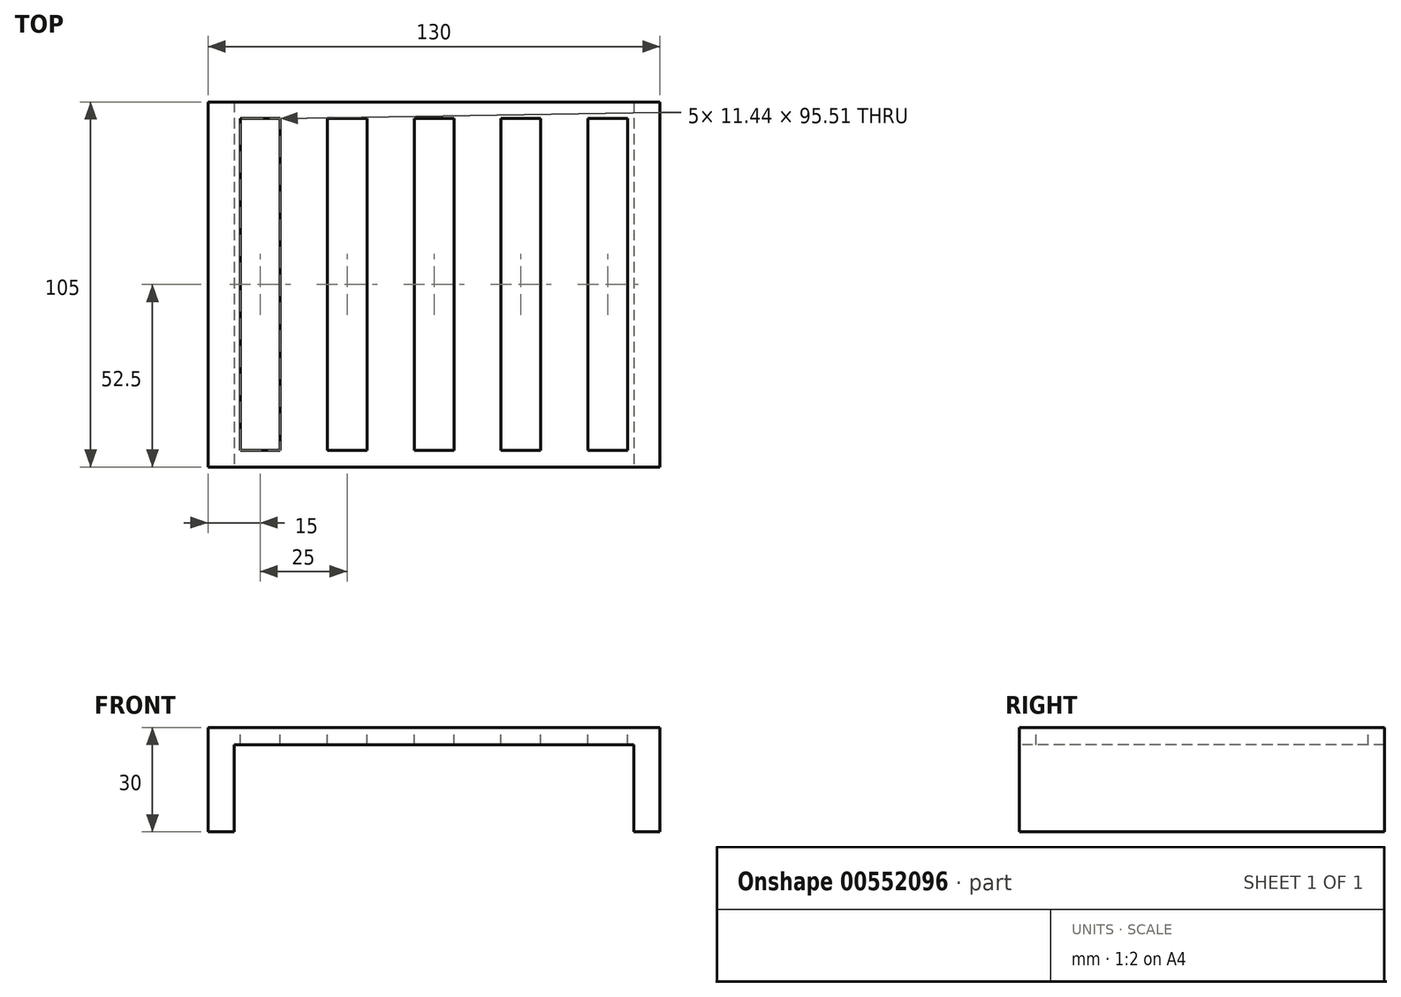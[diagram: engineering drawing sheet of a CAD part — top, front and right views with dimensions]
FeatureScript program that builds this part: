
annotation { "Feature Type Name" : "Feature", "Feature Type Description" : "" }
export const myFeature = defineFeature(function(context is Context, id is Id, definition is map)
    precondition{}
    {
        {
            var Q0;
            Q0=qCreatedBy(makeId("Top.planeOp"),FACE);
            var sketch = newSketch(context, id + "F0", { "sketchPlane" : qUnion([Q0])});
            skLineSegment(sketch, "E0.bottom", {"start": v(-65, 52.5) * mm, "end": v(65, 52.5) * mm});
            skLineSegment(sketch, "E0.top", {"start": v(-65, -52.5) * mm, "end": v(65, -52.5) * mm});
            skLineSegment(sketch, "E0.left", {"start": v(-65, 52.5) * mm, "end": v(-65, -52.5) * mm});
            skLineSegment(sketch, "E0.right", {"start": v(65, 52.5) * mm, "end": v(65, -52.5) * mm});
            skPoint(sketch, "E0.middle", {"position": v(0, 0) * mm});
            skSolve(sketch);
        }
        {
            var Q0;
            Q0=makeQuery(id+"F0.imprint","IMPRINT",FACE,{"disambiguationData":[TD([[makeQuery(id+"F0.imprint","IMPRINT",EDGE,{"derivedFrom":sQuery(id+"F0.wireOp",EDGE,"E0.bottom")}),-1.0]])]});
            extrude(context, id + "F1", {"entities" : qUnion([Q0]), "depth" : 5 * mm, "offsetDistance" : 25 * mm});
        }
        {
            var Q0;
            Q0=makeQuery(id+"F1.opExtrude","CAP_FACE",FACE,{"disambiguationData":[OSD([sQuery(id+"F0.wireOp",EDGE,"E0.bottom"),sQuery(id+"F0.wireOp",EDGE,"E0.top"),sQuery(id+"F0.wireOp",EDGE,"E0.left"),sQuery(id+"F0.wireOp",EDGE,"E0.right")])],"isStart":false});
            var sketch = newSketch(context, id + "F2", { "sketchPlane" : qUnion([Q0])});
            skSolve(sketch);
        }
        {
            var Q0;
            Q0=makeQuery(id+"F1.opExtrude","CAP_FACE",FACE,{"disambiguationData":[OSD([sQuery(id+"F0.wireOp",EDGE,"E0.bottom"),sQuery(id+"F0.wireOp",EDGE,"E0.top"),sQuery(id+"F0.wireOp",EDGE,"E0.left"),sQuery(id+"F0.wireOp",EDGE,"E0.right")])],"isStart":true});
            var sketch = newSketch(context, id + "F3", { "sketchPlane" : qUnion([Q0])});
            skLineSegment(sketch, "E1.bottom", {"start": v(57.5, -33.84) * mm, "end": v(-57.5, -33.84) * mm});
            skLineSegment(sketch, "E1.top", {"start": v(57.5, 33.84) * mm, "end": v(-57.5, 33.84) * mm});
            skLineSegment(sketch, "E1.left", {"start": v(57.5, -33.84) * mm, "end": v(57.5, 33.84) * mm});
            skLineSegment(sketch, "E1.right", {"start": v(-57.5, -33.84) * mm, "end": v(-57.5, 33.84) * mm});
            skPoint(sketch, "E1.middle", {"position": v(0, 0) * mm});
            skLineSegment(sketch, "E2.bottom", {"start": v(65, -52.5) * mm, "end": v(57.5, -52.5) * mm});
            skLineSegment(sketch, "E2.top", {"start": v(65, 52.5) * mm, "end": v(57.5, 52.5) * mm});
            skLineSegment(sketch, "E2.left", {"start": v(65, -52.5) * mm, "end": v(65, 52.5) * mm});
            skLineSegment(sketch, "E2.right", {"start": v(57.5, -52.5) * mm, "end": v(57.5, 52.5) * mm});
            skLineSegment(sketch, "E3.bottom", {"start": v(-65, -52.5) * mm, "end": v(-57.5, -52.5) * mm});
            skLineSegment(sketch, "E3.top", {"start": v(-65, 52.5) * mm, "end": v(-57.5, 52.5) * mm});
            skLineSegment(sketch, "E3.left", {"start": v(-65, -52.5) * mm, "end": v(-65, 52.5) * mm});
            skLineSegment(sketch, "E3.right", {"start": v(-57.5, -52.5) * mm, "end": v(-57.5, 52.5) * mm});
            skSolve(sketch);
        }
        {
            var Q0;
            {var subQ2=sQuery(id+"F3.wireOp",EDGE,"E2.bottom");Q0=makeQuery(id+"F3.imprint","IMPRINT",FACE,{"disambiguationData":[TD([[makeQuery(id+"F3.imprint","IMPRINT",EDGE,{"derivedFrom":subQ2}),1.0]])]});}
            var Q1;
            {var subQ2=sQuery(id+"F3.wireOp",EDGE,"E3.bottom");Q1=makeQuery(id+"F3.imprint","IMPRINT",FACE,{"disambiguationData":[TD([[makeQuery(id+"F3.imprint","IMPRINT",EDGE,{"derivedFrom":subQ2}),1.0]])]});}
            extrude(context, id + "F4", {"entities" : qUnion([Q0, Q1]), "operationType" : NewBodyOperationType.ADD, "depth" : 25 * mm, "offsetDistance" : 25 * mm});
        }
        {
            var Q0;
            Q0=makeQuery(id+"F2.imprint","IMPRINT",FACE,{"disambiguationData":[TD([[makeQuery(id+"F2.imprint","IMPRINT",EDGE,{"derivedFrom":makeQuery(id+"F1.opExtrude","CAP_EDGE",EDGE,{"disambiguationData":[OSD([sQuery(id+"F0.wireOp",EDGE,"E0.bottom")])],"isStart":false})}),-1.0]])]});
            var sketch = newSketch(context, id + "F5", { "sketchPlane" : qUnion([Q0])});
            skLineSegment(sketch, "E4.bottom", {"start": v(-5.72, 47.76) * mm, "end": v(5.72, 47.76) * mm});
            skLineSegment(sketch, "E4.top", {"start": v(-5.72, -47.76) * mm, "end": v(5.72, -47.76) * mm});
            skLineSegment(sketch, "E4.left", {"start": v(-5.72, 47.76) * mm, "end": v(-5.72, -47.76) * mm});
            skLineSegment(sketch, "E4.right", {"start": v(5.72, 47.76) * mm, "end": v(5.72, -47.76) * mm});
            skPoint(sketch, "E4.middle", {"position": v(0, 0) * mm});
            skLineSegment(sketch, "E5.1.0.0", {"start": v(30.72, 47.76) * mm, "end": v(30.72, -47.76) * mm});
            skLineSegment(sketch, "E5.1.0.1", {"start": v(19.28, 47.76) * mm, "end": v(19.28, -47.76) * mm});
            skLineSegment(sketch, "E5.1.0.2", {"start": v(19.28, 47.76) * mm, "end": v(30.72, 47.76) * mm});
            skLineSegment(sketch, "E5.1.0.3", {"start": v(19.28, -47.76) * mm, "end": v(30.72, -47.76) * mm});
            skLineSegment(sketch, "E5.2.0.0", {"start": v(55.72, 47.76) * mm, "end": v(55.72, -47.76) * mm});
            skLineSegment(sketch, "E5.2.0.1", {"start": v(44.28, 47.76) * mm, "end": v(44.28, -47.76) * mm});
            skLineSegment(sketch, "E5.2.0.2", {"start": v(44.28, 47.76) * mm, "end": v(55.72, 47.76) * mm});
            skLineSegment(sketch, "E5.2.0.3", {"start": v(44.28, -47.76) * mm, "end": v(55.72, -47.76) * mm});
            skLineSegment(sketch, "E5.direction1", {"start": v(5.72, -47.76) * mm, "end": v(30.72, -47.76) * mm, "construction": true});
            skLineSegment(sketch, "E6.1.0.0", {"start": v(-30.72, 47.76) * mm, "end": v(-30.72, -47.76) * mm});
            skLineSegment(sketch, "E6.1.0.1", {"start": v(-19.28, 47.76) * mm, "end": v(-19.28, -47.76) * mm});
            skLineSegment(sketch, "E6.1.0.2", {"start": v(-30.72, -47.76) * mm, "end": v(-19.28, -47.76) * mm});
            skLineSegment(sketch, "E6.1.0.3", {"start": v(-30.72, 47.76) * mm, "end": v(-19.28, 47.76) * mm});
            skLineSegment(sketch, "E6.2.0.0", {"start": v(-55.72, 47.76) * mm, "end": v(-55.72, -47.76) * mm});
            skLineSegment(sketch, "E6.2.0.1", {"start": v(-44.28, 47.76) * mm, "end": v(-44.28, -47.76) * mm});
            skLineSegment(sketch, "E6.2.0.2", {"start": v(-55.72, -47.76) * mm, "end": v(-44.28, -47.76) * mm});
            skLineSegment(sketch, "E6.2.0.3", {"start": v(-55.72, 47.76) * mm, "end": v(-44.28, 47.76) * mm});
            skLineSegment(sketch, "E6.direction1", {"start": v(-5.72, -47.76) * mm, "end": v(-30.72, -47.76) * mm, "construction": true});
            skSolve(sketch);
        }
        {
            var Q0;
            Q0 = qSketchRegion(id + "F5", true);
            extrude(context, id + "F6", {"entities" : qUnion([Q0]), "operationType" : NewBodyOperationType.REMOVE, "oppositeDirection" : true, "depth" : 25 * mm, "offsetDistance" : 25 * mm});
        }
    });
